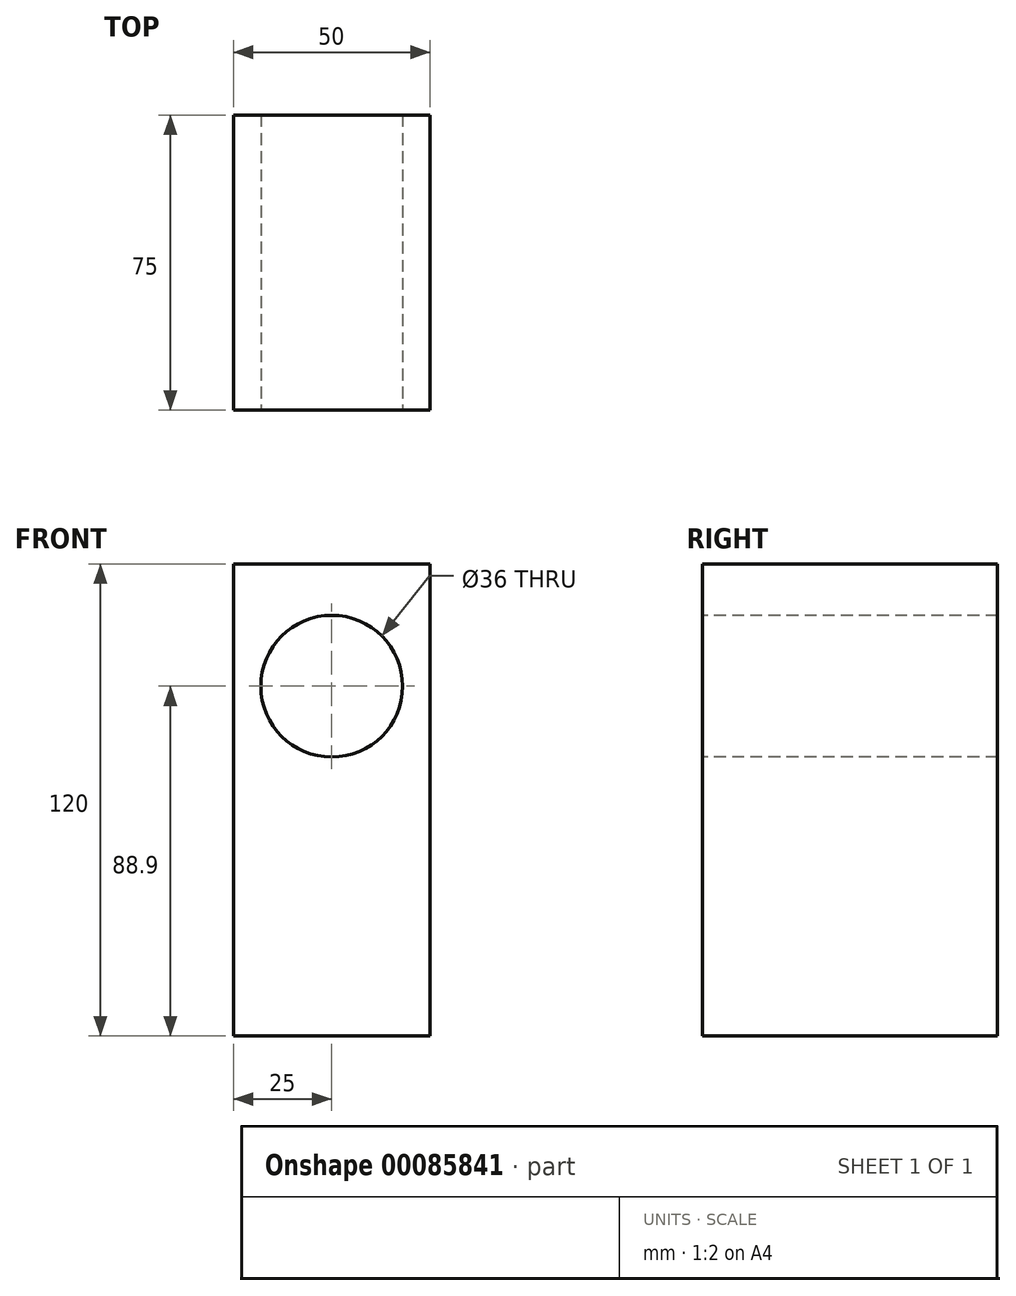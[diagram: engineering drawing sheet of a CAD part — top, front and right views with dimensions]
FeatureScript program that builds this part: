
annotation { "Feature Type Name" : "Feature", "Feature Type Description" : "" }
export const myFeature = defineFeature(function(context is Context, id is Id, definition is map)
    precondition{}
    {
        {
            var Q0;
            Q0=qCreatedBy(makeId("Top.planeOp"),FACE);
            var sketch = newSketch(context, id + "F0", { "sketchPlane" : qUnion([Q0])});
            skLineSegment(sketch, "E0.bottom", {"start": v(25, 37.5) * mm, "end": v(-25, 37.5) * mm});
            skLineSegment(sketch, "E0.top", {"start": v(25, -37.5) * mm, "end": v(-25, -37.5) * mm});
            skLineSegment(sketch, "E0.left", {"start": v(25, 37.5) * mm, "end": v(25, -37.5) * mm});
            skLineSegment(sketch, "E0.right", {"start": v(-25, 37.5) * mm, "end": v(-25, -37.5) * mm});
            skPoint(sketch, "E0.middle", {"position": v(0, 0) * mm});
            skSolve(sketch);
        }
        {
            var Q0;
            Q0 = qSketchRegion(id + "F0", true);
            extrude(context, id + "F1", {"entities" : qUnion([Q0]), "depth" : 120 * mm});
        }
        {
            var Q0;
            Q0=makeQuery(id+"F1.opExtrude","SWEPT_FACE",FACE,{"disambiguationData":[OSD([sQuery(id+"F0.wireOp",EDGE,"E0.top")])]});
            var sketch = newSketch(context, id + "F2", { "sketchPlane" : qUnion([Q0])});
            skCircle(sketch, "E1", {"center": v(0, 88.9) * mm, "radius": 18 * mm});
            skSolve(sketch);
        }
        {
            var Q0;
            Q0 = qSketchRegion(id + "F2", true);
            extrude(context, id + "F3", {"entities" : qUnion([Q0]), "operationType" : NewBodyOperationType.REMOVE, "endBound" : BoundingType.UP_TO_NEXT, "oppositeDirection" : true, "depth" : 25 * mm});
        }
    });
